# Revit family: Bañera Italiana Eco 150X70
name_source: partatom
category: Aparatos sanitarios
revit_build: Autodesk Revit 2017 (Build: 20160225_1515(x64)
units: mm (PartAtom-declared; Revit-internal decimal feet)

## family parameters
Anfitrión = Muro
Compartido = No
Corte con vacíos al cargar = No
Cota de conector redondo = Diámetro de uso
Número OmniClass = 23.45.05.17
Punto de cálculo de habitación = No
Siempre vertical = Sí
Tipo de pieza = Normal
Título OmniClass = Sanitary Leisure Units

## types (2) — shared parameters
zero-valued in all types: Costo

## per-type parameters (varying)
| type | Alto | Ancho | Descripción | Fabricante | Largo | Modelo | Tabla de costo | URL |
| Tipo 1 | 0 mm  [stored 0 ft] | 0 mm  [stored 0 ft] |  |  | 0 mm  [stored 0 ft] |  |  |  |
| Bonaire | 52 mm | 152 mm  [stored 0.498688 ft] | Hidromasaje Bonaire de empotrar lado A | Firplak SA | 183 mm | Bonaire | www.firplak.com/B2B | www.firplak.com |

note: [stored X ft] marks values corroborated as IEEE doubles in the binary element streams (Revit-internal decimal feet)
